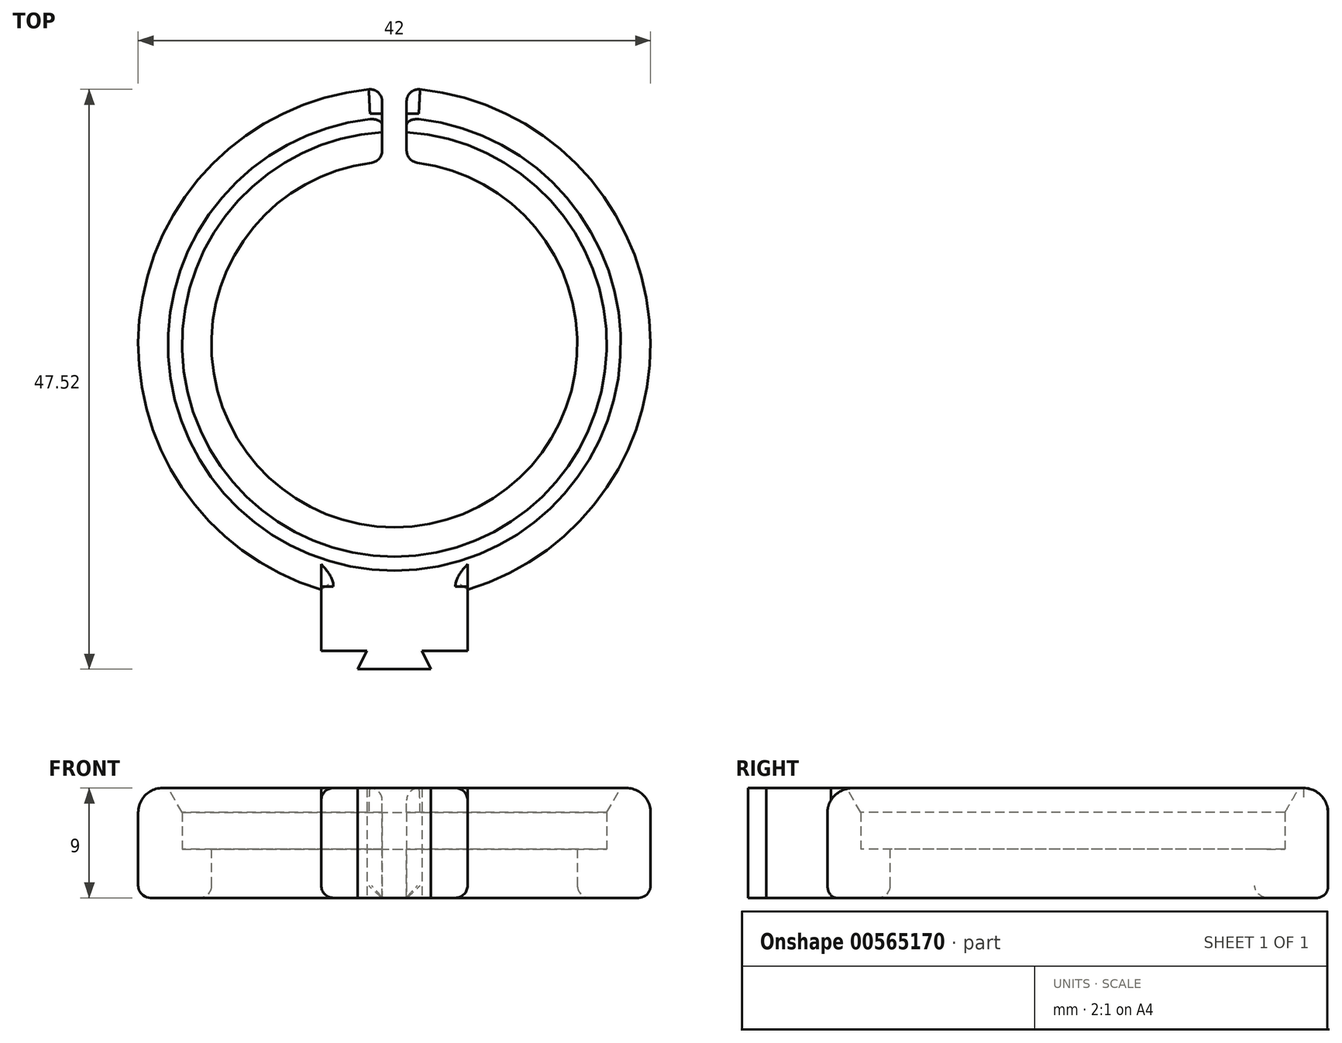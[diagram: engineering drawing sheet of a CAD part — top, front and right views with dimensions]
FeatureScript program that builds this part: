
annotation { "Feature Type Name" : "Feature", "Feature Type Description" : "" }
export const myFeature = defineFeature(function(context is Context, id is Id, definition is map)
    precondition{}
    {
        {
            var Q0;
            Q0=qCreatedBy(makeId("Top.planeOp"),FACE);
            var sketch = newSketch(context, id + "F0", { "sketchPlane" : qUnion([Q0])});
            skLineSegment(sketch, "E0", {"start": v(0, 0) * mm, "end": v(3, 0) * mm});
            skLineSegment(sketch, "E1", {"start": v(3, 0) * mm, "end": v(2.25, 1.5) * mm});
            skLineSegment(sketch, "E2", {"start": v(2.25, 1.5) * mm, "end": v(6, 1.5) * mm});
            skLineSegment(sketch, "E3", {"start": v(6, 1.5) * mm, "end": v(6, 6.5) * mm});
            skLineSegment(sketch, "E4", {"start": v(0, 0) * mm, "end": v(0, 40.88) * mm, "construction": true});
            skLineSegment(sketch, "E5.MirrorCS", {"start": v(0, 0) * mm, "end": v(-3, 0) * mm});
            skLineSegment(sketch, "E6.MirrorCS", {"start": v(-6, 1.5) * mm, "end": v(-6, 6.5) * mm});
            skLineSegment(sketch, "E7.MirrorCS", {"start": v(-2.25, 1.5) * mm, "end": v(-6, 1.5) * mm});
            skLineSegment(sketch, "E8.MirrorCS", {"start": v(-3, 0) * mm, "end": v(-2.25, 1.5) * mm});
            skLineSegment(sketch, "E9", {"start": v(-6, 6.5) * mm, "end": v(6, 6.5) * mm});
            skCircle(sketch, "E10", {"center": v(0, 26.62) * mm, "radius": 21 * mm});
            skCircle(sketch, "E11", {"center": v(0, 26.62) * mm, "radius": 17.4 * mm});
            skCircle(sketch, "E12", {"center": v(0, 26.62) * mm, "radius": 15 * mm});
            skSolve(sketch);
        }
        {
            var Q0;
            Q0=makeQuery(id+"F0.imprint","IMPRINT",FACE,{"disambiguationData":[TD([[makeQuery(id+"F0.imprint","IMPRINT",EDGE,{"derivedFrom":sQuery(id+"F0.wireOp",EDGE,"E0")}),1.0]])]});
            var Q1;
            {var subQ0=sQuery(id+"F0.wireOp",EDGE,"E9");Q1=makeQuery(id+"F0.imprint","IMPRINT",FACE,{"disambiguationData":[TD([[makeQuery(id+"F0.imprint","IMPRINT",EDGE,{"derivedFrom":subQ0}),1.0]])]});}
            var Q2;
            {var subQ0=sQuery(id+"F0.wireOp",EDGE,"E9");Q2=makeQuery(id+"F0.imprint","IMPRINT",FACE,{"disambiguationData":[TD([[makeQuery(id+"F0.imprint","IMPRINT",EDGE,{"derivedFrom":subQ0}),-1.0]])]});}
            extrude(context, id + "F1", {"entities" : qUnion([Q0, Q1, Q2]), "flatOperationType" : FlatOperationType.REMOVE, "depth" : 9 * mm, "offsetDistance" : 25 * mm, "domain" : OperationDomain.MODEL});
        }
        {
            var Q0;
            Q0=makeQuery(id+"F0.imprint","IMPRINT",FACE,{"disambiguationData":[TD([[makeQuery(id+"F0.imprint","IMPRINT",EDGE,{"derivedFrom":sQuery(id+"F0.wireOp",EDGE,"E11")}),1.0]])]});
            extrude(context, id + "F2", {"entities" : qUnion([Q0]), "operationType" : NewBodyOperationType.ADD, "depth" : 4 * mm, "offsetDistance" : 25 * mm});
        }
        {
            var Q0;
            Q0=makeQuery(id+"F1.opExtrude","CAP_FACE",FACE,{"disambiguationData":[OSD([sQuery(id+"F0.wireOp",EDGE,"E0"),sQuery(id+"F0.wireOp",EDGE,"E1"),sQuery(id+"F0.wireOp",EDGE,"E2"),sQuery(id+"F0.wireOp",EDGE,"E3"),sQuery(id+"F0.wireOp",EDGE,"E5.MirrorCS"),sQuery(id+"F0.wireOp",EDGE,"E6.MirrorCS"),sQuery(id+"F0.wireOp",EDGE,"E7.MirrorCS"),sQuery(id+"F0.wireOp",EDGE,"E8.MirrorCS"),sQuery(id+"F0.wireOp",EDGE,"E10"),sQuery(id+"F0.wireOp",EDGE,"E11")])],"isStart":false});
            var sketch = newSketch(context, id + "F3", { "sketchPlane" : qUnion([Q0])});
            skLineSegment(sketch, "E13", {"start": v(0, 0.92) * mm, "end": v(0, 51.95) * mm, "construction": true});
            skPoint(sketch, "E13.endSnap0", {"position": v(0, 47.62) * mm});
            skLineSegment(sketch, "E14.bottom", {"start": v(-1, 40.12) * mm, "end": v(1, 40.12) * mm});
            skLineSegment(sketch, "E14.top", {"start": v(-1, 55.12) * mm, "end": v(1, 55.12) * mm});
            skLineSegment(sketch, "E14.left", {"start": v(-1, 40.12) * mm, "end": v(-1, 55.12) * mm});
            skLineSegment(sketch, "E14.right", {"start": v(1, 40.12) * mm, "end": v(1, 55.12) * mm});
            skSolve(sketch);
        }
        {
            var Q0;
            {var subQ0=sQuery(id+"F3.wireOp",EDGE,"E14.left");var subQ1=makeQuery(id+"F1.opExtrude","CAP_EDGE",EDGE,{"disambiguationData":[OSD([sQuery(id+"F0.wireOp",EDGE,"E10")])],"isStart":false});var subQ2=makeQuery(id+"F3.imprint","INTERSECT",VERTEX,{"derivedFrom":[subQ1,subQ0]});Q0=makeQuery(id+"F3.imprint","IMPRINT",FACE,{"disambiguationData":[TD([[makeQuery(id+"F3.imprint","IMPRINT",EDGE,{"disambiguationData":[TD([[subQ2,1.0]])],"derivedFrom":subQ0}),-1.0]])]});}
            var Q1;
            {var subQ0=sQuery(id+"F3.wireOp",EDGE,"E14.bottom");Q1=makeQuery(id+"F3.imprint","IMPRINT",FACE,{"disambiguationData":[TD([[makeQuery(id+"F3.imprint","IMPRINT",EDGE,{"derivedFrom":subQ0}),1.0]])]});}
            var Q2;
            {var subQ0=sQuery(id+"F3.wireOp",EDGE,"E14.top");Q2=makeQuery(id+"F3.imprint","IMPRINT",FACE,{"disambiguationData":[TD([[makeQuery(id+"F3.imprint","IMPRINT",EDGE,{"derivedFrom":subQ0}),-1.0]])]});}
            extrude(context, id + "F4", {"entities" : qUnion([Q0, Q1, Q2]), "operationType" : NewBodyOperationType.REMOVE, "oppositeDirection" : true, "depth" : 25 * mm, "offsetDistance" : 25 * mm});
        }
        {
            var Q0;
            Q0=makeQuery(id+"F1.opExtrude","CAP_EDGE",EDGE,{"disambiguationData":[OSD([sQuery(id+"F0.wireOp",EDGE,"E11")])],"isStart":false});
            chamfer(context, id + "F5", {"entities" : qUnion([Q0]), "chamferType" : ChamferType.OFFSET_ANGLE, "width" : 2 * mm, "oppositeDirection" : false, "angle" : 30 * degree, "tangentPropagation" : true});
        }
        {
            var Q0;
            {var subQ0=sQuery(id+"F0.wireOp",EDGE,"E10");var subQ1=sQuery(id+"F0.wireOp",EDGE,"E3");Q0=makeQuery(id+"F4.boolean.opBoolean","SPLIT",EDGE,{"disambiguationData":[TD([makeQuery(id+"F1.opExtrude","SWEPT_FACE",FACE,{"disambiguationData":[OSD([subQ1])]})])],"derivedFrom":makeQuery(id+"F1.opExtrude","CAP_EDGE",EDGE,{"disambiguationData":[OSD([subQ0])],"isStart":false})});}
            var Q1;
            {var subQ0=sQuery(id+"F0.wireOp",EDGE,"E10");var subQ1=sQuery(id+"F0.wireOp",EDGE,"E6.MirrorCS");Q1=makeQuery(id+"F4.boolean.opBoolean","SPLIT",EDGE,{"disambiguationData":[TD([makeQuery(id+"F1.opExtrude","SWEPT_FACE",FACE,{"disambiguationData":[OSD([subQ1])]})])],"derivedFrom":makeQuery(id+"F1.opExtrude","CAP_EDGE",EDGE,{"disambiguationData":[OSD([subQ0])],"isStart":false})});}
            fillet(context, id + "F6", {"entities" : qUnion([Q0, Q1]), "radius" : 2 * mm, "tangentPropagation" : true, "allowEdgeOverflow" : false});
        }
        {
            var Q0;
            {var subQ1=sQuery(id+"F0.wireOp",EDGE,"E3");var subQ2=sQuery(id+"F0.wireOp",EDGE,"E10");Q0=makeQuery(id+"F4.boolean.opBoolean","SPLIT",EDGE,{"disambiguationData":[TD([makeQuery(id+"F1.opExtrude","SWEPT_FACE",FACE,{"disambiguationData":[OSD([subQ1])]})])],"derivedFrom":makeQuery(id+"F1.opExtrude","CAP_EDGE",EDGE,{"disambiguationData":[OSD([subQ2])],"isStart":true})});}
            var Q1;
            Q1=makeQuery(id+"F2.opExtrude","CAP_EDGE",EDGE,{"disambiguationData":[OSD([sQuery(id+"F0.wireOp",EDGE,"E12")])],"isStart":true});
            var Q2;
            {var subQ1=sQuery(id+"F0.wireOp",EDGE,"E10");var subQ2=sQuery(id+"F0.wireOp",EDGE,"E6.MirrorCS");Q2=makeQuery(id+"F4.boolean.opBoolean","SPLIT",EDGE,{"disambiguationData":[TD([makeQuery(id+"F1.opExtrude","SWEPT_FACE",FACE,{"disambiguationData":[OSD([subQ2])]})])],"derivedFrom":makeQuery(id+"F1.opExtrude","CAP_EDGE",EDGE,{"disambiguationData":[OSD([subQ1])],"isStart":true})});}
            var Q3;
            Q3=makeQuery(id+"F1.opExtrude","CAP_EDGE",EDGE,{"disambiguationData":[OSD([sQuery(id+"F0.wireOp",EDGE,"E6.MirrorCS")])],"isStart":false});
            var Q4;
            Q4=makeQuery(id+"F1.opExtrude","CAP_EDGE",EDGE,{"disambiguationData":[OSD([sQuery(id+"F0.wireOp",EDGE,"E3")])],"isStart":false});
            var Q5;
            Q5=makeQuery(id+"F1.opExtrude","CAP_EDGE",EDGE,{"disambiguationData":[OSD([sQuery(id+"F0.wireOp",EDGE,"E6.MirrorCS")])],"isStart":true});
            var Q6;
            Q6=makeQuery(id+"F1.opExtrude","CAP_EDGE",EDGE,{"disambiguationData":[OSD([sQuery(id+"F0.wireOp",EDGE,"E3")])],"isStart":true});
            var Q7;
            Q7=makeQuery(id+"F4.boolean.opBoolean","INTERSECT",EDGE,{"derivedFrom":[makeQuery(id+"F2.opExtrude","SWEPT_FACE",FACE,{"disambiguationData":[OSD([sQuery(id+"F0.wireOp",EDGE,"E12")])]}),makeQuery(id+"F4.opExtrude","SWEPT_FACE",FACE,{"disambiguationData":[OSD([sQuery(id+"F3.wireOp",EDGE,"E14.left")])]})]});
            var Q8;
            Q8=makeQuery(id+"F4.boolean.opBoolean","INTERSECT",EDGE,{"derivedFrom":[makeQuery(id+"F2.opExtrude","SWEPT_FACE",FACE,{"disambiguationData":[OSD([sQuery(id+"F0.wireOp",EDGE,"E12")])]}),makeQuery(id+"F4.opExtrude","SWEPT_FACE",FACE,{"disambiguationData":[OSD([sQuery(id+"F3.wireOp",EDGE,"E14.right")])]})]});
            var Q9;
            Q9=makeQuery(id+"F4.boolean.opBoolean","INTERSECT",EDGE,{"derivedFrom":[makeQuery(id+"F1.opExtrude","SWEPT_FACE",FACE,{"disambiguationData":[OSD([sQuery(id+"F0.wireOp",EDGE,"E10")])]}),makeQuery(id+"F4.opExtrude","SWEPT_FACE",FACE,{"disambiguationData":[OSD([sQuery(id+"F3.wireOp",EDGE,"E14.left")])]})]});
            var Q10;
            Q10=makeQuery(id+"F4.boolean.opBoolean","INTERSECT",EDGE,{"derivedFrom":[makeQuery(id+"F1.opExtrude","SWEPT_FACE",FACE,{"disambiguationData":[OSD([sQuery(id+"F0.wireOp",EDGE,"E10")])]}),makeQuery(id+"F4.opExtrude","SWEPT_FACE",FACE,{"disambiguationData":[OSD([sQuery(id+"F3.wireOp",EDGE,"E14.right")])]})]});
            fillet(context, id + "F7", {"entities" : qUnion([Q0, Q1, Q2, Q3, Q4, Q5, Q6, Q7, Q8, Q9, Q10]), "radius" : 1 * mm, "tangentPropagation" : true, "allowEdgeOverflow" : false});
        }
    });
